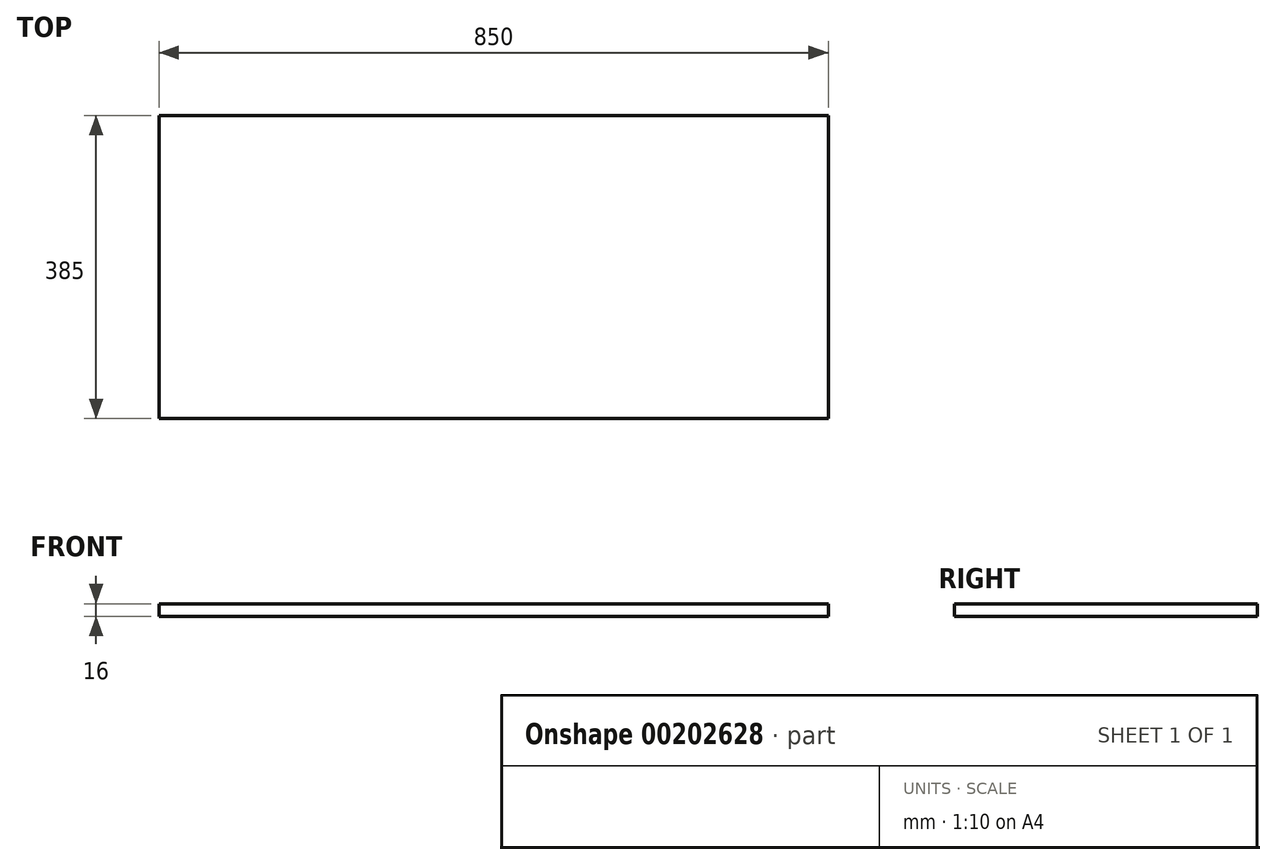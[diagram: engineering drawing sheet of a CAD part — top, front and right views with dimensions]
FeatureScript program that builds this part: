
annotation { "Feature Type Name" : "Feature", "Feature Type Description" : "" }
export const myFeature = defineFeature(function(context is Context, id is Id, definition is map)
    precondition{}
    {
        {
            var Q0;
            Q0=qCreatedBy(makeId("Top.planeOp"),FACE);
            var sketch = newSketch(context, id + "F0", { "sketchPlane" : qUnion([Q0])});
            skLineSegment(sketch, "E0.bottom", {"start": v(-864.34, -235.28) * mm, "end": v(-14.34, -235.28) * mm});
            skLineSegment(sketch, "E0.top", {"start": v(-864.34, 149.72) * mm, "end": v(-14.34, 149.72) * mm});
            skLineSegment(sketch, "E0.left", {"start": v(-864.34, -235.28) * mm, "end": v(-864.34, 149.72) * mm});
            skLineSegment(sketch, "E0.right", {"start": v(-14.34, -235.28) * mm, "end": v(-14.34, 149.72) * mm});
            skSolve(sketch);
        }
        {
            var Q0;
            Q0=makeQuery(id+"F0.imprint","IMPRINT",FACE,{"disambiguationData":[TD([[makeQuery(id+"F0.imprint","IMPRINT",EDGE,{"derivedFrom":sQuery(id+"F0.wireOp",EDGE,"E0.bottom")}),1.0]])]});
            extrude(context, id + "F1", {"entities" : qUnion([Q0]), "depth" : 16 * mm});
        }
    });
